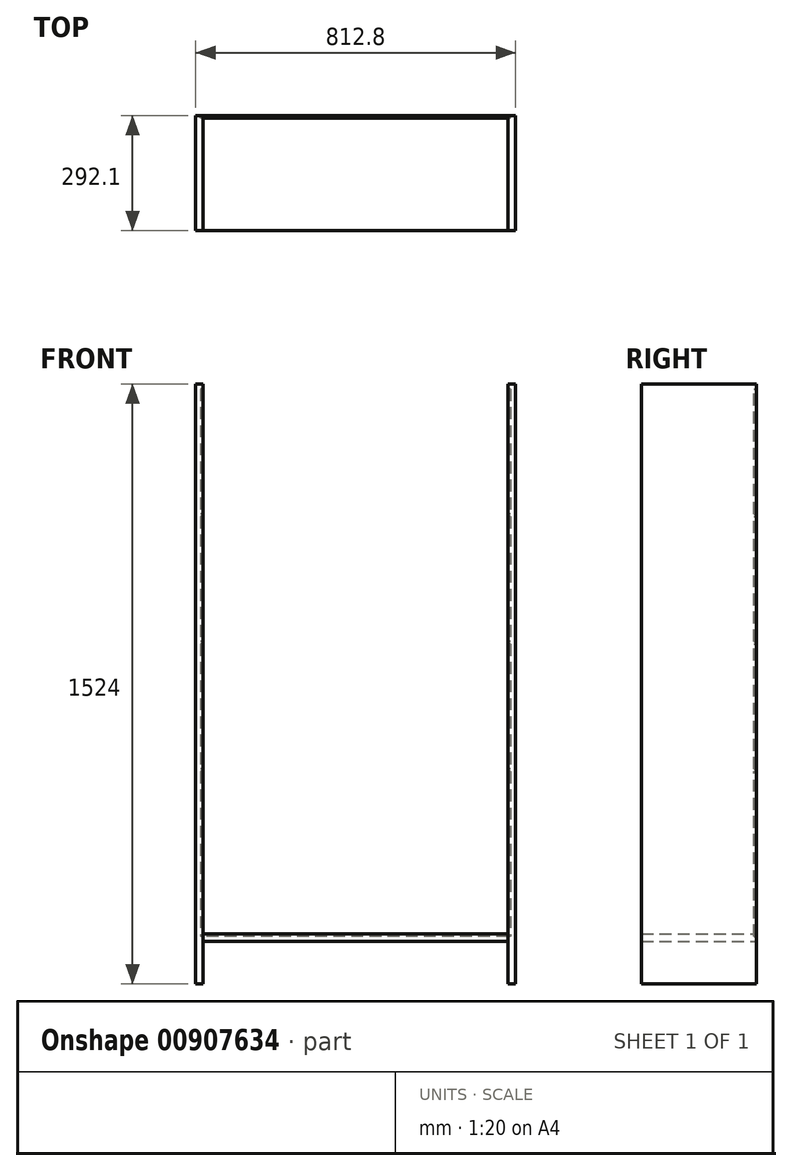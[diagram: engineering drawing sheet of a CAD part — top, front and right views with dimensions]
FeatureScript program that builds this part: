
annotation { "Feature Type Name" : "Feature", "Feature Type Description" : "" }
export const myFeature = defineFeature(function(context is Context, id is Id, definition is map)
    precondition{}
    {
        {
            var Q0;
            Q0=qCreatedBy(makeId("Front.planeOp"),FACE);
            var sketch = newSketch(context, id + "F0", { "sketchPlane" : qUnion([Q0])});
            skLineSegment(sketch, "E0.bottom", {"start": v(406.4, -762) * mm, "end": v(-406.4, -762) * mm});
            skLineSegment(sketch, "E0.top", {"start": v(406.4, 762) * mm, "end": v(-406.4, 762) * mm});
            skLineSegment(sketch, "E0.left", {"start": v(406.4, -762) * mm, "end": v(406.4, 762) * mm});
            skLineSegment(sketch, "E0.right", {"start": v(-406.4, -762) * mm, "end": v(-406.4, 762) * mm});
            skPoint(sketch, "E0.middle", {"position": v(0, 0) * mm});
            skLineSegment(sketch, "E1.bottom", {"start": v(-406.4, 762) * mm, "end": v(-387.35, 762) * mm});
            skLineSegment(sketch, "E1.top", {"start": v(-406.4, -762) * mm, "end": v(-387.35, -762) * mm});
            skLineSegment(sketch, "E1.left", {"start": v(-406.4, 762) * mm, "end": v(-406.4, -762) * mm});
            skLineSegment(sketch, "E1.right", {"start": v(-387.35, 762) * mm, "end": v(-387.35, -762) * mm});
            skLineSegment(sketch, "E2.bottom", {"start": v(406.4, 762) * mm, "end": v(387.35, 762) * mm});
            skLineSegment(sketch, "E2.top", {"start": v(406.4, -762) * mm, "end": v(387.35, -762) * mm});
            skLineSegment(sketch, "E2.left", {"start": v(406.4, 762) * mm, "end": v(406.4, -762) * mm});
            skLineSegment(sketch, "E2.right", {"start": v(387.35, 762) * mm, "end": v(387.35, -762) * mm});
            skLineSegment(sketch, "E3.bottom", {"start": v(-387.35, 762) * mm, "end": v(387.35, 762) * mm});
            skLineSegment(sketch, "E3.top", {"start": v(-387.35, 742.95) * mm, "end": v(387.35, 742.95) * mm});
            skLineSegment(sketch, "E3.left", {"start": v(-387.35, 762) * mm, "end": v(-387.35, 742.95) * mm});
            skLineSegment(sketch, "E3.right", {"start": v(387.35, 762) * mm, "end": v(387.35, 742.95) * mm});
            skLineSegment(sketch, "E4", {"start": v(0, 742.95) * mm, "end": v(0, 438.15) * mm});
            skLineSegment(sketch, "E5.bottom", {"start": v(-387.35, 438.15) * mm, "end": v(387.35, 438.15) * mm});
            skLineSegment(sketch, "E5.top", {"start": v(-387.35, 419.1) * mm, "end": v(387.35, 419.1) * mm});
            skLineSegment(sketch, "E5.left", {"start": v(-387.35, 438.15) * mm, "end": v(-387.35, 419.1) * mm});
            skLineSegment(sketch, "E5.right", {"start": v(387.35, 438.15) * mm, "end": v(387.35, 419.1) * mm});
            skLineSegment(sketch, "E6", {"start": v(0, 419.1) * mm, "end": v(0, 114.3) * mm});
            skLineSegment(sketch, "E7.bottom", {"start": v(-387.35, 114.3) * mm, "end": v(387.35, 114.3) * mm});
            skLineSegment(sketch, "E7.top", {"start": v(-387.35, 95.25) * mm, "end": v(387.35, 95.25) * mm});
            skLineSegment(sketch, "E7.left", {"start": v(-387.35, 114.3) * mm, "end": v(-387.35, 95.25) * mm});
            skLineSegment(sketch, "E7.right", {"start": v(387.35, 114.3) * mm, "end": v(387.35, 95.25) * mm});
            skLineSegment(sketch, "E8", {"start": v(0, 95.25) * mm, "end": v(0, -209.55) * mm});
            skLineSegment(sketch, "E9.bottom", {"start": v(-387.35, -209.55) * mm, "end": v(387.35, -209.55) * mm});
            skLineSegment(sketch, "E9.top", {"start": v(-387.35, -228.6) * mm, "end": v(387.35, -228.6) * mm});
            skLineSegment(sketch, "E9.left", {"start": v(-387.35, -209.55) * mm, "end": v(-387.35, -228.6) * mm});
            skLineSegment(sketch, "E9.right", {"start": v(387.35, -209.55) * mm, "end": v(387.35, -228.6) * mm});
            skLineSegment(sketch, "E10", {"start": v(0, -228.6) * mm, "end": v(0, -635) * mm});
            skLineSegment(sketch, "E11.bottom", {"start": v(-387.35, -635) * mm, "end": v(387.35, -635) * mm});
            skLineSegment(sketch, "E11.top", {"start": v(-387.35, -654.05) * mm, "end": v(387.35, -654.05) * mm});
            skLineSegment(sketch, "E11.left", {"start": v(-387.35, -635) * mm, "end": v(-387.35, -654.05) * mm});
            skLineSegment(sketch, "E11.right", {"start": v(387.35, -635) * mm, "end": v(387.35, -654.05) * mm});
            skSolve(sketch);
        }
        {
            var Q0;
            Q0=makeQuery(id+"F0.imprint","IMPRINT",FACE,{"disambiguationData":[TD([[makeQuery(id+"F0.imprint","IMPRINT",EDGE,{"derivedFrom":sQuery(id+"F0.wireOp",EDGE,"E3.bottom")}),-1.0]])]});
            var Q1;
            {var subQ4=sQuery(id+"F0.wireOp",EDGE,"E5.left");Q1=makeQuery(id+"F0.imprint","IMPRINT",FACE,{"disambiguationData":[TD([[makeQuery(id+"F0.imprint","IMPRINT",EDGE,{"derivedFrom":subQ4}),1.0]])]});}
            var Q2;
            {var subQ4=sQuery(id+"F0.wireOp",EDGE,"E7.left");Q2=makeQuery(id+"F0.imprint","IMPRINT",FACE,{"disambiguationData":[TD([[makeQuery(id+"F0.imprint","IMPRINT",EDGE,{"derivedFrom":subQ4}),1.0]])]});}
            var Q3;
            {var subQ4=sQuery(id+"F0.wireOp",EDGE,"E9.left");Q3=makeQuery(id+"F0.imprint","IMPRINT",FACE,{"disambiguationData":[TD([[makeQuery(id+"F0.imprint","IMPRINT",EDGE,{"derivedFrom":subQ4}),1.0]])]});}
            var Q4;
            Q4=makeQuery(id+"F0.imprint","IMPRINT",FACE,{"disambiguationData":[TD([[makeQuery(id+"F0.imprint","IMPRINT",EDGE,{"derivedFrom":sQuery(id+"F0.wireOp",EDGE,"E11.top")}),1.0]])]});
            extrude(context, id + "F1", {"entities" : qUnion([Q0, Q1, Q2, Q3, Q4]), "depth" : 292.1 * mm, "offsetDistance" : 25.4 * mm});
        }
        {
            var Q0;
            Q0=qCreatedBy(makeId("Front.planeOp"),FACE);
            var sketch = newSketch(context, id + "F2", { "sketchPlane" : qUnion([Q0])});
            skPoint(sketch, "E12.0", {"position": v(-387.35, 762) * mm});
            skPoint(sketch, "E13.0", {"position": v(-387.35, -654.05) * mm});
            skPoint(sketch, "E14.0", {"position": v(387.35, -654.05) * mm});
            skPoint(sketch, "E15.0", {"position": v(387.35, 742.95) * mm});
            skPoint(sketch, "E16.0", {"position": v(387.35, 762) * mm});
            skLineSegment(sketch, "E17.bottom", {"start": v(-387.35, 762) * mm, "end": v(-406.4, 762) * mm});
            skLineSegment(sketch, "E17.top", {"start": v(-387.35, -762) * mm, "end": v(-406.4, -762) * mm});
            skLineSegment(sketch, "E17.left", {"start": v(-387.35, 762) * mm, "end": v(-387.35, -762) * mm});
            skLineSegment(sketch, "E17.right", {"start": v(-406.4, 762) * mm, "end": v(-406.4, -762) * mm});
            skLineSegment(sketch, "E18.bottom", {"start": v(387.35, 762) * mm, "end": v(406.4, 762) * mm});
            skLineSegment(sketch, "E18.top", {"start": v(387.35, -762) * mm, "end": v(406.4, -762) * mm});
            skLineSegment(sketch, "E18.left", {"start": v(387.35, 762) * mm, "end": v(387.35, -762) * mm});
            skLineSegment(sketch, "E18.right", {"start": v(406.4, 762) * mm, "end": v(406.4, -762) * mm});
            skSolve(sketch);
        }
        {
            var Q0;
            Q0=makeQuery(id+"F2.imprint","IMPRINT",FACE,{"disambiguationData":[TD([[makeQuery(id+"F2.imprint","IMPRINT",EDGE,{"derivedFrom":sQuery(id+"F2.wireOp",EDGE,"E17.bottom")}),1.0]])]});
            var Q1;
            Q1=makeQuery(id+"F2.imprint","IMPRINT",FACE,{"disambiguationData":[TD([[makeQuery(id+"F2.imprint","IMPRINT",EDGE,{"derivedFrom":sQuery(id+"F2.wireOp",EDGE,"E18.bottom")}),-1.0]])]});
            extrude(context, id + "F3", {"entities" : qUnion([Q0, Q1]), "depth" : 292.1 * mm, "offsetDistance" : 25.4 * mm});
        }
        {
            var Q0;
            Q0=makeQuery(id+"F3.opExtrude","CAP_FACE",FACE,{"disambiguationData":[OSD([sQuery(id+"F2.wireOp",EDGE,"E18.bottom"),sQuery(id+"F2.wireOp",EDGE,"E18.top"),sQuery(id+"F2.wireOp",EDGE,"E18.left"),sQuery(id+"F2.wireOp",EDGE,"E18.right")])],"isStart":true});
            var sketch = newSketch(context, id + "F4", { "sketchPlane" : qUnion([Q0])});
            skPoint(sketch, "E19.0", {"position": v(-387.35, 742.95) * mm});
            skPoint(sketch, "E20.0", {"position": v(387.35, 438.15) * mm});
            skPoint(sketch, "E21.0", {"position": v(-387.35, 419.1) * mm});
            skPoint(sketch, "E22.0", {"position": v(387.35, 114.3) * mm});
            skPoint(sketch, "E23.0", {"position": v(-387.35, 95.25) * mm});
            skPoint(sketch, "E24.0", {"position": v(387.35, -209.55) * mm});
            skPoint(sketch, "E25.0", {"position": v(-387.35, -228.6) * mm});
            skPoint(sketch, "E26.0", {"position": v(387.35, -635) * mm});
            skLineSegment(sketch, "E27.bottom", {"start": v(-387.35, 742.95) * mm, "end": v(387.35, 742.95) * mm});
            skLineSegment(sketch, "E27.top", {"start": v(-387.35, 438.15) * mm, "end": v(387.35, 438.15) * mm});
            skLineSegment(sketch, "E27.left", {"start": v(-387.35, 742.95) * mm, "end": v(-387.35, 438.15) * mm});
            skLineSegment(sketch, "E27.right", {"start": v(387.35, 742.95) * mm, "end": v(387.35, 438.15) * mm});
            skLineSegment(sketch, "E28.0", {"start": v(-393.7, 749.3) * mm, "end": v(393.7, 749.3) * mm});
            skLineSegment(sketch, "E28.1", {"start": v(-393.7, 749.3) * mm, "end": v(-393.7, 431.8) * mm});
            skLineSegment(sketch, "E28.2", {"start": v(-393.7, 431.8) * mm, "end": v(393.7, 431.8) * mm});
            skLineSegment(sketch, "E28.3", {"start": v(393.7, 749.3) * mm, "end": v(393.7, 431.8) * mm});
            skLineSegment(sketch, "E29.bottom", {"start": v(-387.35, 419.1) * mm, "end": v(387.35, 419.1) * mm});
            skLineSegment(sketch, "E29.top", {"start": v(-387.35, 114.3) * mm, "end": v(387.35, 114.3) * mm});
            skLineSegment(sketch, "E29.left", {"start": v(-387.35, 419.1) * mm, "end": v(-387.35, 114.3) * mm});
            skLineSegment(sketch, "E29.right", {"start": v(387.35, 419.1) * mm, "end": v(387.35, 114.3) * mm});
            skLineSegment(sketch, "E30.0", {"start": v(-393.7, 425.45) * mm, "end": v(-393.7, 107.95) * mm});
            skLineSegment(sketch, "E30.1", {"start": v(-393.7, 425.45) * mm, "end": v(393.7, 425.45) * mm});
            skLineSegment(sketch, "E30.2", {"start": v(393.7, 425.45) * mm, "end": v(393.7, 107.95) * mm});
            skLineSegment(sketch, "E30.3", {"start": v(-393.7, 107.95) * mm, "end": v(393.7, 107.95) * mm});
            skLineSegment(sketch, "E31.bottom", {"start": v(-387.35, 95.25) * mm, "end": v(387.35, 95.25) * mm});
            skLineSegment(sketch, "E31.top", {"start": v(-387.35, -209.55) * mm, "end": v(387.35, -209.55) * mm});
            skLineSegment(sketch, "E31.left", {"start": v(-387.35, 95.25) * mm, "end": v(-387.35, -209.55) * mm});
            skLineSegment(sketch, "E31.right", {"start": v(387.35, 95.25) * mm, "end": v(387.35, -209.55) * mm});
            skLineSegment(sketch, "E32.0", {"start": v(-393.7, 101.6) * mm, "end": v(393.7, 101.6) * mm});
            skLineSegment(sketch, "E32.1", {"start": v(-393.7, 101.6) * mm, "end": v(-393.7, -215.9) * mm});
            skLineSegment(sketch, "E32.2", {"start": v(-393.7, -215.9) * mm, "end": v(393.7, -215.9) * mm});
            skLineSegment(sketch, "E32.3", {"start": v(393.7, 101.6) * mm, "end": v(393.7, -215.9) * mm});
            skLineSegment(sketch, "E33.bottom", {"start": v(-387.35, -228.6) * mm, "end": v(387.35, -228.6) * mm});
            skLineSegment(sketch, "E33.top", {"start": v(-387.35, -635) * mm, "end": v(387.35, -635) * mm});
            skLineSegment(sketch, "E33.left", {"start": v(-387.35, -228.6) * mm, "end": v(-387.35, -635) * mm});
            skLineSegment(sketch, "E33.right", {"start": v(387.35, -228.6) * mm, "end": v(387.35, -635) * mm});
            skLineSegment(sketch, "E34.0", {"start": v(-393.7, -222.25) * mm, "end": v(393.7, -222.25) * mm});
            skLineSegment(sketch, "E34.1", {"start": v(-393.7, -222.25) * mm, "end": v(-393.7, -641.35) * mm});
            skLineSegment(sketch, "E34.2", {"start": v(-393.7, -641.35) * mm, "end": v(393.7, -641.35) * mm});
            skLineSegment(sketch, "E34.3", {"start": v(393.7, -222.25) * mm, "end": v(393.7, -641.35) * mm});
            skSolve(sketch);
        }
        {
            var Q0;
            Q0 = qSketchRegion(id + "F4", true);
            extrude(context, id + "F5", {"entities" : qUnion([Q0]), "operationType" : NewBodyOperationType.REMOVE, "oppositeDirection" : true, "depth" : 6.35 * mm, "offsetDistance" : 25.4 * mm});
        }
    });
